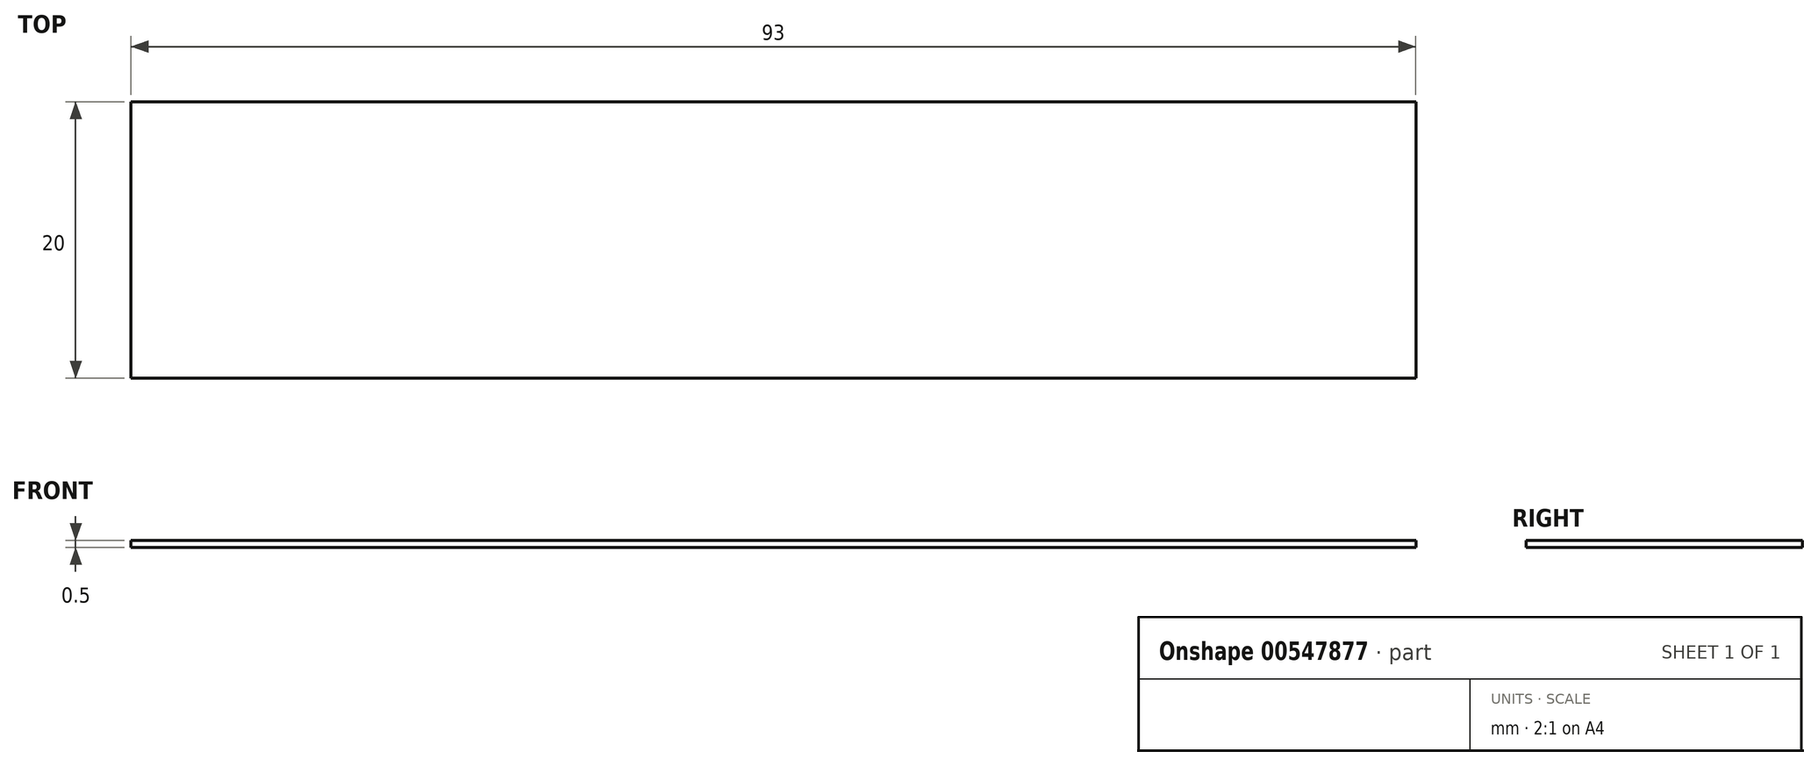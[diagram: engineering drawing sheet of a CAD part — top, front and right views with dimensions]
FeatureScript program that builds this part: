
annotation { "Feature Type Name" : "Feature", "Feature Type Description" : "" }
export const myFeature = defineFeature(function(context is Context, id is Id, definition is map)
    precondition{}
    {
        {
            var Q0;
            Q0=qCreatedBy(makeId("Top.planeOp"),FACE);
            var sketch = newSketch(context, id + "F0", { "sketchPlane" : qUnion([Q0])});
            skLineSegment(sketch, "E0.bottom", {"start": v(-44.94, -14.78) * mm, "end": v(48.06, -14.78) * mm});
            skLineSegment(sketch, "E0.top", {"start": v(-44.94, -34.78) * mm, "end": v(48.06, -34.78) * mm});
            skLineSegment(sketch, "E0.left", {"start": v(-44.94, -14.78) * mm, "end": v(-44.94, -34.78) * mm});
            skLineSegment(sketch, "E0.right", {"start": v(48.06, -14.78) * mm, "end": v(48.06, -34.78) * mm});
            skSolve(sketch);
        }
        {
            var Q0;
            Q0=makeQuery(id+"F0.imprint","IMPRINT",FACE,{"disambiguationData":[TD([[makeQuery(id+"F0.imprint","IMPRINT",EDGE,{"derivedFrom":sQuery(id+"F0.wireOp",EDGE,"E0.bottom")}),-1.0]])]});
            extrude(context, id + "F1", {"entities" : qUnion([Q0]), "depth" : 0.5 * mm, "offsetDistance" : 25 * mm});
        }
    });
